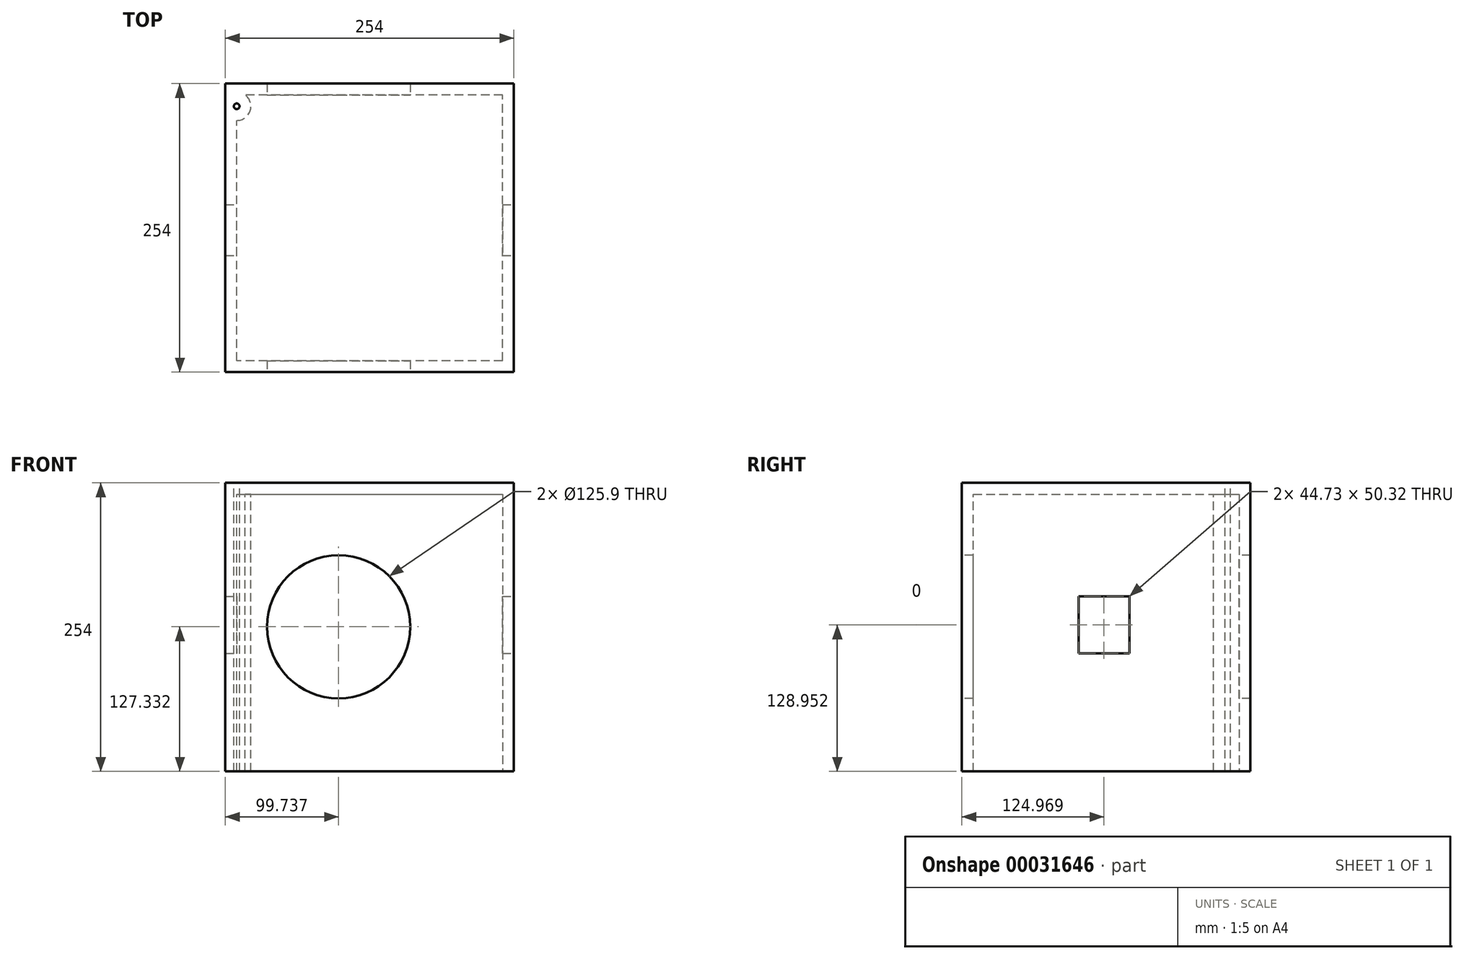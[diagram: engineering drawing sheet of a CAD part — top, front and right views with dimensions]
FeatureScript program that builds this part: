
annotation { "Feature Type Name" : "Feature", "Feature Type Description" : "" }
export const myFeature = defineFeature(function(context is Context, id is Id, definition is map)
    precondition{}
    {
        {
            var Q0;
            Q0=qCreatedBy(makeId("Front.planeOp"),FACE);
            var sketch = newSketch(context, id + "F0", { "sketchPlane" : qUnion([Q0])});
            skLineSegment(sketch, "E0", {"start": v(0, 0) * mm, "end": v(0, 254) * mm});
            skLineSegment(sketch, "E1", {"start": v(0, 254) * mm, "end": v(254, 254) * mm});
            skLineSegment(sketch, "E2", {"start": v(254, 254) * mm, "end": v(254, 0) * mm});
            skLineSegment(sketch, "E3", {"start": v(254, 0) * mm, "end": v(0, 0) * mm});
            skSolve(sketch);
        }
        {
            var Q0;
            Q0 = qSketchRegion(id + "F0", true);
            extrude(context, id + "F1", {"entities" : qUnion([Q0]), "depth" : 254 * mm});
        }
        {
            var Q0;
            Q0=makeQuery(id+"F1.opExtrude","SWEPT_FACE",FACE,{"disambiguationData":[OSD([sQuery(id+"F0.wireOp",EDGE,"E1")])]});
            var sketch = newSketch(context, id + "F2", { "sketchPlane" : qUnion([Q0])});
            skPoint(sketch, "E4", {"position": v(10, -20) * mm});
            skSolve(sketch);
        }
        {
            var Q0;
            Q0=sQuery(id+"F2.wireOp",VERTEX,"E4");
            var Q1;
            Q1=makeQuery(id+"F1.opExtrude","SWEPT_BODY",BODY,{"disambiguationData":[OSD([sQuery(id+"F0.wireOp",EDGE,"E0"),sQuery(id+"F0.wireOp",EDGE,"E1"),sQuery(id+"F0.wireOp",EDGE,"E2"),sQuery(id+"F0.wireOp",EDGE,"E3")])]});
            hole(context, id + "F3", {"style" : HoleStyle.SIMPLE, "holeDiameter" : 5 * mm, "endStyle" : HoleEndStyle.THROUGH, "locations" : qUnion([Q0]), "scope" : qUnion([Q1])});
        }
        {
            var Q0;
            Q0=makeQuery(id+"F1.opExtrude","SWEPT_FACE",FACE,{"disambiguationData":[OSD([sQuery(id+"F0.wireOp",EDGE,"E3")])]});
            shell(context, id + "F4", {"entities" : qUnion([Q0]), "thickness" : 10 * mm});
        }
        {
            var Q0;
            Q0=makeQuery(id+"F1.opExtrude","CAP_FACE",FACE,{"disambiguationData":[OSD([sQuery(id+"F0.wireOp",EDGE,"E0"),sQuery(id+"F0.wireOp",EDGE,"E1"),sQuery(id+"F0.wireOp",EDGE,"E2"),sQuery(id+"F0.wireOp",EDGE,"E3")])],"isStart":false});
            var sketch = newSketch(context, id + "F5", { "sketchPlane" : qUnion([Q0])});
            skCircle(sketch, "E5", {"center": v(99.74, 127.33) * mm, "radius": 62.95 * mm});
            skSolve(sketch);
        }
        {
            var Q0;
            Q0 = qSketchRegion(id + "F5", true);
            extrude(context, id + "F6", {"entities" : qUnion([Q0]), "operationType" : NewBodyOperationType.REMOVE, "endBound" : BoundingType.THROUGH_ALL, "oppositeDirection" : true, "depth" : 25 * mm});
        }
        {
            var Q0;
            Q0=makeQuery(id+"F1.opExtrude","SWEPT_FACE",FACE,{"disambiguationData":[OSD([sQuery(id+"F0.wireOp",EDGE,"E2")])]});
            var sketch = newSketch(context, id + "F7", { "sketchPlane" : qUnion([Q0])});
            skLineSegment(sketch, "E6.bottom", {"start": v(-106.66, 103.79) * mm, "end": v(-151.4, 103.79) * mm});
            skLineSegment(sketch, "E6.top", {"start": v(-106.66, 154.11) * mm, "end": v(-151.4, 154.11) * mm});
            skLineSegment(sketch, "E6.left", {"start": v(-106.66, 103.79) * mm, "end": v(-106.66, 154.11) * mm});
            skLineSegment(sketch, "E6.right", {"start": v(-151.4, 103.79) * mm, "end": v(-151.4, 154.11) * mm});
            skSolve(sketch);
        }
        {
            var Q0;
            Q0 = qSketchRegion(id + "F7", true);
            extrude(context, id + "F8", {"entities" : qUnion([Q0]), "operationType" : NewBodyOperationType.REMOVE, "endBound" : BoundingType.THROUGH_ALL, "oppositeDirection" : true, "depth" : 25 * mm});
        }
    });
